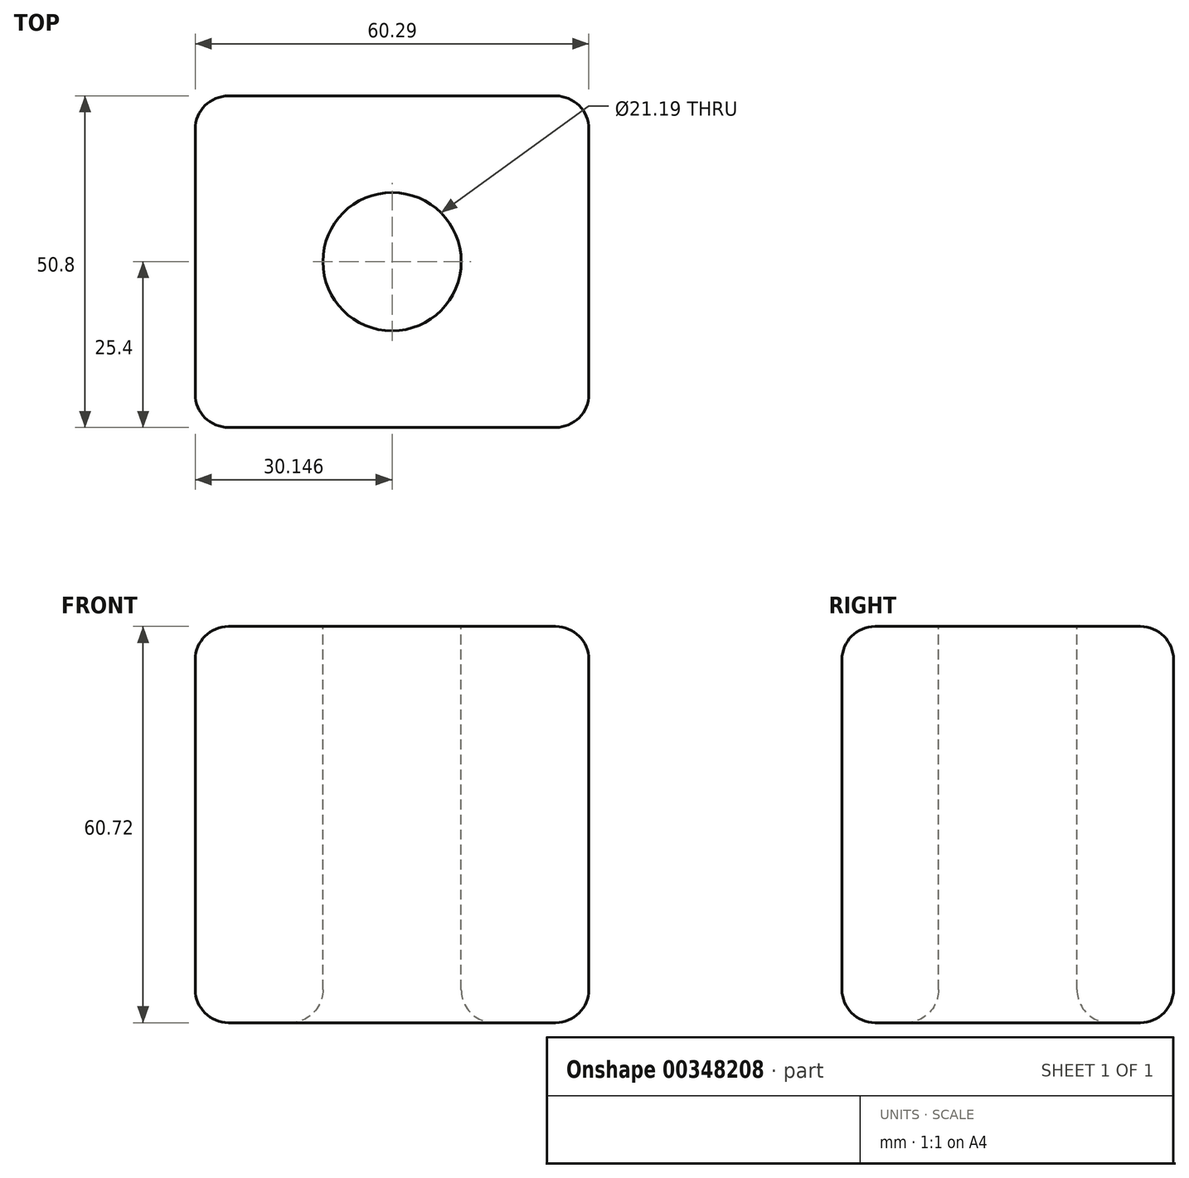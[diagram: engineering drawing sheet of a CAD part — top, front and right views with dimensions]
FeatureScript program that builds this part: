
annotation { "Feature Type Name" : "Feature", "Feature Type Description" : "" }
export const myFeature = defineFeature(function(context is Context, id is Id, definition is map)
    precondition{}
    {
        {
            var Q0;
            Q0=qCreatedBy(makeId("Front.planeOp"),FACE);
            var sketch = newSketch(context, id + "F0", { "sketchPlane" : qUnion([Q0])});
            skLineSegment(sketch, "E0.bottom", {"start": v(0, 0) * mm, "end": v(60.3, 0) * mm});
            skLineSegment(sketch, "E0.top", {"start": v(0, 60.72) * mm, "end": v(60.3, 60.72) * mm});
            skLineSegment(sketch, "E0.left", {"start": v(0, 0) * mm, "end": v(0, 60.72) * mm});
            skLineSegment(sketch, "E0.right", {"start": v(60.3, 0) * mm, "end": v(60.3, 60.72) * mm});
            skSolve(sketch);
        }
        {
            var Q0;
            Q0=makeQuery(id+"F0.imprint","IMPRINT",FACE,{"disambiguationData":[TD([[makeQuery(id+"F0.imprint","IMPRINT",EDGE,{"derivedFrom":sQuery(id+"F0.wireOp",EDGE,"E0.bottom")}),1.0]])]});
            extrude(context, id + "F1", {"entities" : qUnion([Q0]), "depth" : 50.8 * mm});
        }
        {
            var Q0;
            Q0=makeQuery(id+"F1.opExtrude","SWEPT_FACE",FACE,{"disambiguationData":[OSD([sQuery(id+"F0.wireOp",EDGE,"E0.top")])]});
            var sketch = newSketch(context, id + "F2", { "sketchPlane" : qUnion([Q0])});
            skCircle(sketch, "E1", {"center": v(30.15, -25.4) * mm, "radius": 10.6 * mm});
            skPoint(sketch, "E1.centerSnap0", {"position": v(30.15, -50.8) * mm});
            skPoint(sketch, "E1.centerSnap1", {"position": v(60.3, -25.4) * mm});
            skSolve(sketch);
        }
        {
            var Q0;
            Q0 = qSketchRegion(id + "F2", true);
            extrude(context, id + "F3", {"entities" : qUnion([Q0]), "operationType" : NewBodyOperationType.REMOVE, "endBound" : BoundingType.UP_TO_NEXT, "oppositeDirection" : true, "depth" : 25.4 * mm});
        }
        {
            var Q0;
            Q0=makeQuery(id+"F1.opExtrude","CAP_EDGE",EDGE,{"disambiguationData":[OSD([sQuery(id+"F0.wireOp",EDGE,"E0.right")])],"isStart":true});
            fillet(context, id + "F4", {"entities" : qUnion([Q0]), "radius" : 5.08 * mm, "tangentPropagation" : true, "allowEdgeOverflow" : false});
        }
        {
            var Q0;
            Q0=makeQuery(id+"F1.opExtrude","CAP_EDGE",EDGE,{"disambiguationData":[OSD([sQuery(id+"F0.wireOp",EDGE,"E0.top")])],"isStart":true});
            var Q1;
            Q1=makeQuery(id+"F1.opExtrude","CAP_EDGE",EDGE,{"disambiguationData":[OSD([sQuery(id+"F0.wireOp",EDGE,"E0.bottom")])],"isStart":true});
            var Q2;
            Q2=makeQuery(id+"F1.opExtrude","CAP_EDGE",EDGE,{"disambiguationData":[OSD([sQuery(id+"F0.wireOp",EDGE,"E0.left")])],"isStart":true});
            var Q3;
            Q3=makeQuery(id+"F3.boolean.opBoolean","COPY",EDGE,{"derivedFrom":makeQuery(id+"F3.opExtrude","CAP_EDGE",EDGE,{"disambiguationData":[OSD([sQuery(id+"F2.wireOp",EDGE,"E1")])],"isStart":true})});
            var Q4;
            Q4=makeQuery(id+"F1.opExtrude","CAP_EDGE",EDGE,{"disambiguationData":[OSD([sQuery(id+"F0.wireOp",EDGE,"E0.top")])],"isStart":false});
            var Q5;
            Q5=makeQuery(id+"F1.opExtrude","SWEPT_EDGE",EDGE,{"disambiguationData":[OSD([sQuery(id+"F0.wireOp",EDGE,"E0.top"),sQuery(id+"F0.wireOp",EDGE,"E0.left")])]});
            var Q6;
            Q6=makeQuery(id+"F1.opExtrude","CAP_EDGE",EDGE,{"disambiguationData":[OSD([sQuery(id+"F0.wireOp",EDGE,"E0.left")])],"isStart":false});
            var Q7;
            Q7=makeQuery(id+"F1.opExtrude","SWEPT_EDGE",EDGE,{"disambiguationData":[OSD([sQuery(id+"F0.wireOp",EDGE,"E0.bottom"),sQuery(id+"F0.wireOp",EDGE,"E0.left")])]});
            var Q8;
            Q8=makeQuery(id+"F1.opExtrude","SWEPT_FACE",FACE,{"disambiguationData":[OSD([sQuery(id+"F0.wireOp",EDGE,"E0.right")])]});
            var Q9;
            Q9=makeQuery(id+"F1.opExtrude","SWEPT_FACE",FACE,{"disambiguationData":[OSD([sQuery(id+"F0.wireOp",EDGE,"E0.bottom")])]});
            fillet(context, id + "F5", {"entities" : qUnion([Q0, Q1, Q2, Q3, Q4, Q5, Q6, Q7, Q8, Q9]), "radius" : 5.08 * mm, "tangentPropagation" : true, "allowEdgeOverflow" : false});
        }
    });
